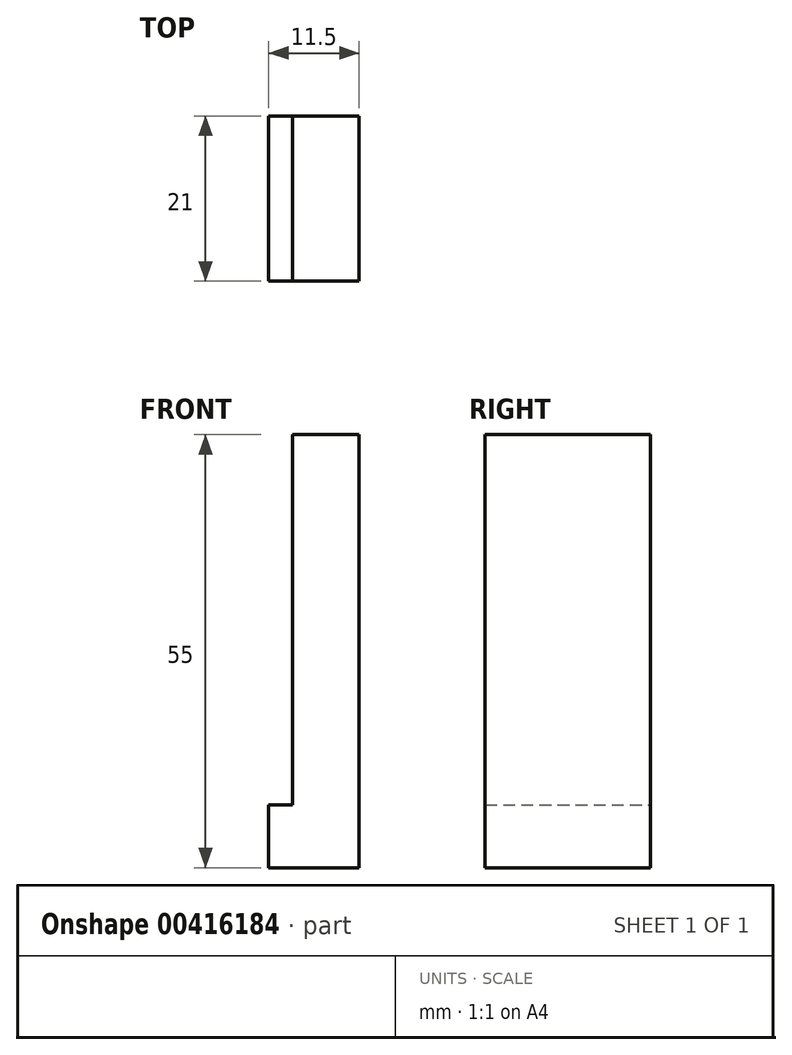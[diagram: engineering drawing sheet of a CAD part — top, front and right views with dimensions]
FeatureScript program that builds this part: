
annotation { "Feature Type Name" : "Feature", "Feature Type Description" : "" }
export const myFeature = defineFeature(function(context is Context, id is Id, definition is map)
    precondition{}
    {
        {
            var Q0;
            Q0=qCreatedBy(makeId("Front.planeOp"),FACE);
            var sketch = newSketch(context, id + "F0", { "sketchPlane" : qUnion([Q0])});
            skLineSegment(sketch, "E0.bottom", {"start": v(-64.38, -1.29) * mm, "end": v(-55.88, -1.29) * mm});
            skLineSegment(sketch, "E0.top", {"start": v(-64.38, -56.29) * mm, "end": v(-55.88, -56.29) * mm});
            skLineSegment(sketch, "E0.left", {"start": v(-64.38, -1.29) * mm, "end": v(-64.38, -48.29) * mm});
            skLineSegment(sketch, "E0.right", {"start": v(-55.88, -1.29) * mm, "end": v(-55.88, -56.29) * mm});
            skLineSegment(sketch, "E1.bottom", {"start": v(-55.88, -56.29) * mm, "end": v(-67.38, -56.29) * mm});
            skLineSegment(sketch, "E1.top", {"start": v(-64.38, -48.29) * mm, "end": v(-67.38, -48.29) * mm});
            skLineSegment(sketch, "E1.left", {"start": v(-55.88, -56.29) * mm, "end": v(-55.88, -48.29) * mm});
            skLineSegment(sketch, "E1.right", {"start": v(-67.38, -56.29) * mm, "end": v(-67.38, -48.29) * mm});
            skSolve(sketch);
        }
        {
            var Q0;
            Q0=makeQuery(id+"F0.imprint","IMPRINT",FACE,{"disambiguationData":[TD([[makeQuery(id+"F0.imprint","IMPRINT",EDGE,{"derivedFrom":sQuery(id+"F0.wireOp",EDGE,"E0.bottom")}),-1.0]])]});
            extrude(context, id + "F1", {"entities" : qUnion([Q0]), "depth" : 21 * mm});
        }
    });
